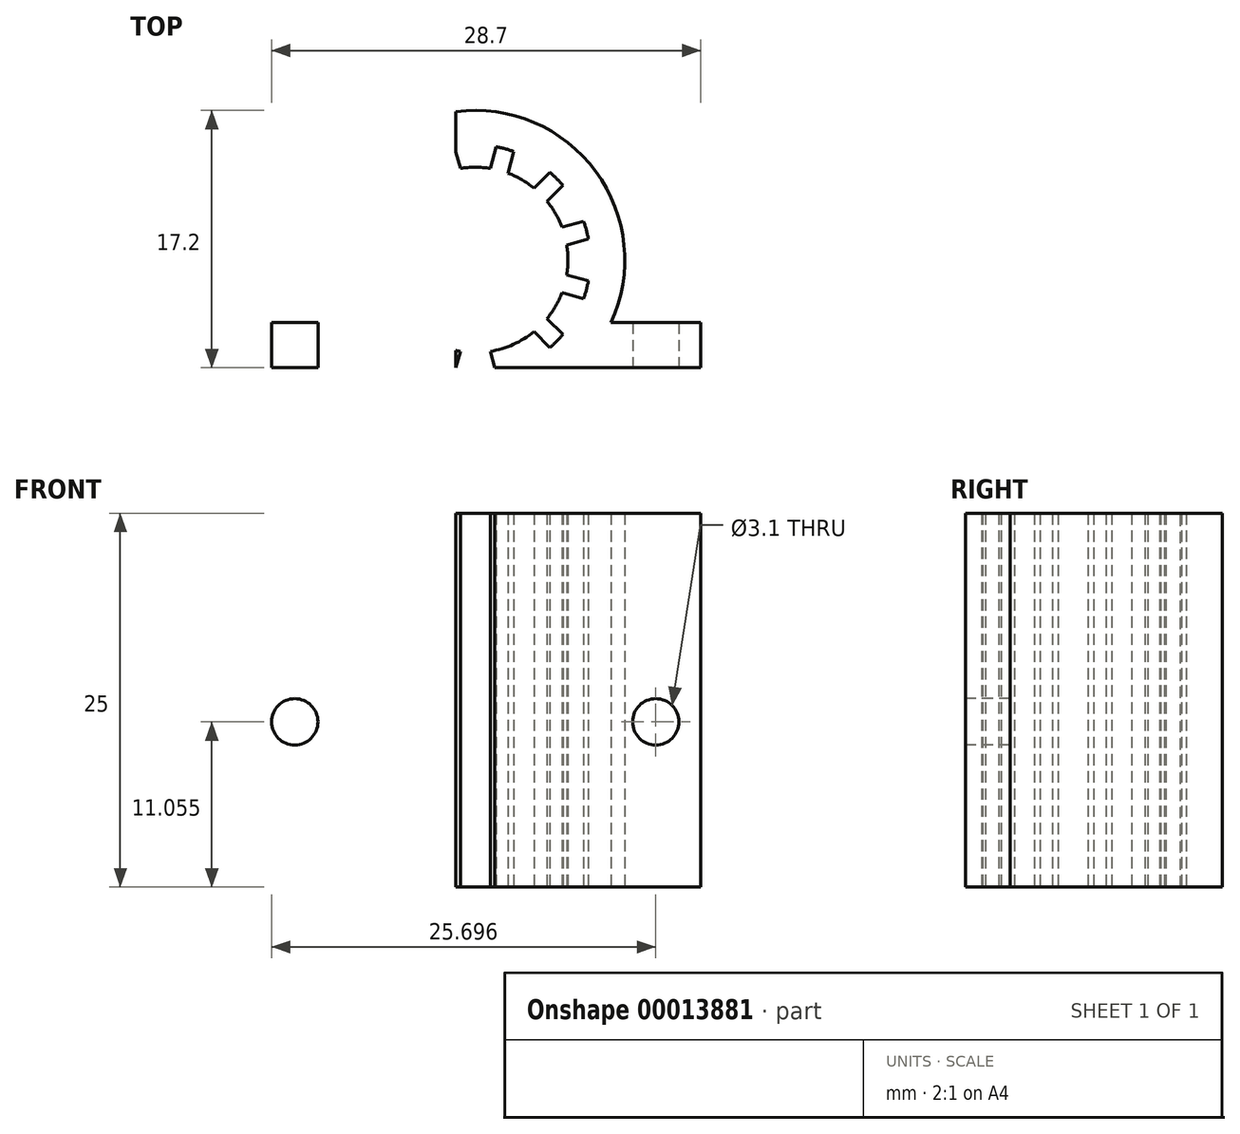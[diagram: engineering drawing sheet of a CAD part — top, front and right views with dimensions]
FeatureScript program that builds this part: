
annotation { "Feature Type Name" : "Feature", "Feature Type Description" : "" }
export const myFeature = defineFeature(function(context is Context, id is Id, definition is map)
    precondition{}
    {
        {
            var Q0;
            Q0=qCreatedBy(makeId("Top.planeOp"),FACE);
            var sketch = newSketch(context, id + "F0", { "sketchPlane" : qUnion([Q0])});
            skCircle(sketch, "E0", {"center": v(-45.8, 26.19) * mm, "radius": 10 * mm});
            skCircle(sketch, "E1", {"center": v(-45.8, 26.19) * mm, "radius": 6.2 * mm});
            skLineSegment(sketch, "E2", {"start": v(-53.65, 19.99) * mm, "end": v(-37.95, 19.99) * mm, "construction": true});
            skLineSegment(sketch, "E3", {"start": v(-45.8, 19.99) * mm, "end": v(-45.8, 38.7) * mm, "construction": true});
            skLineSegment(sketch, "E4", {"start": v(-47.19, 33.76) * mm, "end": v(-46.8, 32.3) * mm});
            skCircle(sketch, "E5", {"center": v(-45.8, 26.19) * mm, "radius": 7.7 * mm, "construction": true});
            skLineSegment(sketch, "E6.MirrorCS", {"start": v(-44.41, 33.76) * mm, "end": v(-44.8, 32.3) * mm});
            skCircle(sketch, "E7.MirrorC", {"center": v(-45.8, 26.19) * mm, "radius": 7.7 * mm});
            skLineSegment(sketch, "E8.1.0", {"start": v(-50.79, 32.05) * mm, "end": v(-49.72, 30.99) * mm});
            skLineSegment(sketch, "E8.1.1", {"start": v(-48.38, 33.44) * mm, "end": v(-48, 31.99) * mm});
            skLineSegment(sketch, "E8.2.0", {"start": v(-53.05, 28.77) * mm, "end": v(-51.6, 28.38) * mm});
            skLineSegment(sketch, "E8.2.1", {"start": v(-51.66, 31.17) * mm, "end": v(-50.6, 30.11) * mm});
            skLineSegment(sketch, "E8.3.0", {"start": v(-53.37, 24.8) * mm, "end": v(-51.92, 25.19) * mm});
            skLineSegment(sketch, "E8.3.1", {"start": v(-53.37, 27.58) * mm, "end": v(-51.92, 27.19) * mm});
            skLineSegment(sketch, "E8.4.0", {"start": v(-51.66, 21.2) * mm, "end": v(-50.6, 22.26) * mm});
            skLineSegment(sketch, "E8.4.1", {"start": v(-53.05, 23.6) * mm, "end": v(-51.6, 24) * mm});
            skLineSegment(sketch, "E8.5.0", {"start": v(-48.38, 18.94) * mm, "end": v(-48, 20.39) * mm});
            skLineSegment(sketch, "E8.5.1", {"start": v(-50.79, 20.33) * mm, "end": v(-49.72, 21.39) * mm});
            skLineSegment(sketch, "E8.6.0", {"start": v(-44.41, 18.62) * mm, "end": v(-44.8, 20.07) * mm});
            skLineSegment(sketch, "E8.6.1", {"start": v(-47.19, 18.62) * mm, "end": v(-46.8, 20.07) * mm});
            skLineSegment(sketch, "E8.7.0", {"start": v(-40.81, 20.33) * mm, "end": v(-41.87, 21.39) * mm});
            skLineSegment(sketch, "E8.7.1", {"start": v(-43.22, 18.94) * mm, "end": v(-43.6, 20.39) * mm});
            skLineSegment(sketch, "E9", {"start": v(-52.74, 18.99) * mm, "end": v(-38.86, 18.99) * mm});
            skLineSegment(sketch, "E10", {"start": v(-52.74, 18.99) * mm, "end": v(-60.87, 18.99) * mm});
            skLineSegment(sketch, "E11", {"start": v(-60.87, 18.99) * mm, "end": v(-60.87, 21.99) * mm});
            skLineSegment(sketch, "E12", {"start": v(-60.87, 21.99) * mm, "end": v(-54.87, 21.99) * mm});
            skLineSegment(sketch, "E13.MirrorCS", {"start": v(-30.72, 21.99) * mm, "end": v(-36.72, 21.99) * mm});
            skLineSegment(sketch, "E14.MirrorCS", {"start": v(-30.72, 18.99) * mm, "end": v(-30.72, 21.99) * mm});
            skLineSegment(sketch, "E15.MirrorCS", {"start": v(-38.86, 18.99) * mm, "end": v(-30.72, 18.99) * mm});
            skLineSegment(sketch, "E16.2.8.0", {"start": v(-38.55, 23.6) * mm, "end": v(-40, 24) * mm});
            skLineSegment(sketch, "E16.3.8.0", {"start": v(-39.94, 21.2) * mm, "end": v(-41, 22.26) * mm});
            skLineSegment(sketch, "E16.2.9.0", {"start": v(-38.23, 27.58) * mm, "end": v(-39.68, 27.19) * mm});
            skLineSegment(sketch, "E16.3.9.0", {"start": v(-38.23, 24.8) * mm, "end": v(-39.68, 25.19) * mm});
            skLineSegment(sketch, "E16.2.10.0", {"start": v(-39.94, 31.17) * mm, "end": v(-41, 30.11) * mm});
            skLineSegment(sketch, "E16.3.10.0", {"start": v(-38.55, 28.77) * mm, "end": v(-40, 28.38) * mm});
            skLineSegment(sketch, "E16.2.11.0", {"start": v(-43.22, 33.44) * mm, "end": v(-43.6, 31.99) * mm});
            skLineSegment(sketch, "E16.3.11.0", {"start": v(-40.81, 32.05) * mm, "end": v(-41.87, 30.99) * mm});
            skSolve(sketch);
        }
        {
            var Q0;
            {var subQ1=sQuery(id+"F0.wireOp",EDGE,"E10");Q0=makeQuery(id+"F0.imprint","IMPRINT",FACE,{"disambiguationData":[TD([[makeQuery(id+"F0.imprint","IMPRINT",EDGE,{"derivedFrom":subQ1}),-1.0]])]});}
            var Q1;
            {var subQ3=sQuery(id+"F0.wireOp",EDGE,"E0");var subQ8=makeQuery(id+"F0.imprint","INTERSECT",VERTEX,{"derivedFrom":[subQ3,sQuery(id+"F0.wireOp",EDGE,"E12")]});Q1=makeQuery(id+"F0.imprint","IMPRINT",FACE,{"disambiguationData":[TD([[makeQuery(id+"F0.imprint","IMPRINT",EDGE,{"disambiguationData":[TD([[subQ8,1.0]])],"derivedFrom":subQ3}),1.0]])]});}
            var Q2;
            {var subQ1=sQuery(id+"F0.wireOp",EDGE,"E13.MirrorCS");Q2=makeQuery(id+"F0.imprint","IMPRINT",FACE,{"disambiguationData":[TD([[makeQuery(id+"F0.imprint","IMPRINT",EDGE,{"derivedFrom":subQ1}),1.0]])]});}
            var Q3;
            {var subQ1=sQuery(id+"F0.wireOp",EDGE,"E8.4.0");Q3=makeQuery(id+"F0.imprint","IMPRINT",FACE,{"disambiguationData":[TD([[makeQuery(id+"F0.imprint","IMPRINT",EDGE,{"derivedFrom":subQ1}),1.0]])]});}
            var Q4;
            {var subQ1=sQuery(id+"F0.wireOp",EDGE,"E8.3.0");Q4=makeQuery(id+"F0.imprint","IMPRINT",FACE,{"disambiguationData":[TD([[makeQuery(id+"F0.imprint","IMPRINT",EDGE,{"derivedFrom":subQ1}),1.0]])]});}
            var Q5;
            {var subQ1=sQuery(id+"F0.wireOp",EDGE,"E8.2.0");Q5=makeQuery(id+"F0.imprint","IMPRINT",FACE,{"disambiguationData":[TD([[makeQuery(id+"F0.imprint","IMPRINT",EDGE,{"derivedFrom":subQ1}),1.0]])]});}
            var Q6;
            {var subQ1=sQuery(id+"F0.wireOp",EDGE,"E8.1.0");Q6=makeQuery(id+"F0.imprint","IMPRINT",FACE,{"disambiguationData":[TD([[makeQuery(id+"F0.imprint","IMPRINT",EDGE,{"derivedFrom":subQ1}),1.0]])]});}
            var Q7;
            {var subQ2=sQuery(id+"F0.wireOp",EDGE,"E4");Q7=makeQuery(id+"F0.imprint","IMPRINT",FACE,{"disambiguationData":[TD([[makeQuery(id+"F0.imprint","IMPRINT",EDGE,{"derivedFrom":subQ2}),1.0]])]});}
            var Q8;
            {var subQ1=sQuery(id+"F0.wireOp",EDGE,"E16.2.11.0");Q8=makeQuery(id+"F0.imprint","IMPRINT",FACE,{"disambiguationData":[TD([[makeQuery(id+"F0.imprint","IMPRINT",EDGE,{"derivedFrom":subQ1}),1.0]])]});}
            var Q9;
            {var subQ1=sQuery(id+"F0.wireOp",EDGE,"E16.2.10.0");Q9=makeQuery(id+"F0.imprint","IMPRINT",FACE,{"disambiguationData":[TD([[makeQuery(id+"F0.imprint","IMPRINT",EDGE,{"derivedFrom":subQ1}),1.0]])]});}
            var Q10;
            {var subQ1=sQuery(id+"F0.wireOp",EDGE,"E16.2.9.0");Q10=makeQuery(id+"F0.imprint","IMPRINT",FACE,{"disambiguationData":[TD([[makeQuery(id+"F0.imprint","IMPRINT",EDGE,{"derivedFrom":subQ1}),1.0]])]});}
            var Q11;
            {var subQ1=sQuery(id+"F0.wireOp",EDGE,"E16.2.8.0");Q11=makeQuery(id+"F0.imprint","IMPRINT",FACE,{"disambiguationData":[TD([[makeQuery(id+"F0.imprint","IMPRINT",EDGE,{"derivedFrom":subQ1}),1.0]])]});}
            var Q12;
            {var subQ7=sQuery(id+"F0.wireOp",EDGE,"E8.7.0");Q12=makeQuery(id+"F0.imprint","IMPRINT",FACE,{"disambiguationData":[TD([[makeQuery(id+"F0.imprint","IMPRINT",EDGE,{"derivedFrom":subQ7}),1.0]])]});}
            var Q13;
            {var subQ5=sQuery(id+"F0.wireOp",EDGE,"E8.5.1");Q13=makeQuery(id+"F0.imprint","IMPRINT",FACE,{"disambiguationData":[TD([[makeQuery(id+"F0.imprint","IMPRINT",EDGE,{"derivedFrom":subQ5}),-1.0]])]});}
            var Q14;
            {var subQ3=sQuery(id+"F0.wireOp",EDGE,"E8.6.0");var subQ5=sQuery(id+"F0.wireOp",EDGE,"E1");var subQ7=makeQuery(id+"F0.imprint","INTERSECT",VERTEX,{"derivedFrom":[subQ5,subQ3]});Q14=makeQuery(id+"F0.imprint","IMPRINT",FACE,{"disambiguationData":[TD([[makeQuery(id+"F0.imprint","IMPRINT",EDGE,{"disambiguationData":[TD([[subQ7,-1.0]])],"derivedFrom":subQ5}),-1.0]])]});}
            var Q15;
            {var subQ3=sQuery(id+"F0.wireOp",EDGE,"E8.5.0");var subQ5=sQuery(id+"F0.wireOp",EDGE,"E1");var subQ7=makeQuery(id+"F0.imprint","INTERSECT",VERTEX,{"derivedFrom":[subQ5,subQ3]});Q15=makeQuery(id+"F0.imprint","IMPRINT",FACE,{"disambiguationData":[TD([[makeQuery(id+"F0.imprint","IMPRINT",EDGE,{"disambiguationData":[TD([[subQ7,-1.0]])],"derivedFrom":subQ5}),-1.0]])]});}
            extrude(context, id + "F1", {"entities" : qUnion([Q0, Q1, Q2, Q3, Q4, Q5, Q6, Q7, Q8, Q9, Q10, Q11, Q12, Q13, Q14, Q15]), "depth" : 25 * mm});
        }
        {
            var Q0;
            Q0=makeQuery(id+"F1.opExtrude","SWEPT_FACE",FACE,{"disambiguationData":[OSD([sQuery(id+"F0.wireOp",EDGE,"E9"),sQuery(id+"F0.wireOp",EDGE,"E10")])]});
            var sketch = newSketch(context, id + "F2", { "sketchPlane" : qUnion([Q0])});
            skLineSegment(sketch, "E17.0", {"start": v(-44.8, 25) * mm, "end": v(-46.8, 25) * mm});
            skLineSegment(sketch, "E18", {"start": v(-45.8, 25) * mm, "end": v(-45.8, 35.27) * mm, "construction": true});
            skCircle(sketch, "E19", {"center": v(-57.87, 21.07) * mm, "radius": 1.55 * mm});
            skLineSegment(sketch, "E20.0", {"start": v(-60.87, 25) * mm, "end": v(-54.87, 25) * mm});
            skLineSegment(sketch, "E21", {"start": v(-57.87, 25) * mm, "end": v(-57.87, 21.07) * mm, "construction": true});
            skCircle(sketch, "E22.MirrorC", {"center": v(-33.72, 21.07) * mm, "radius": 1.55 * mm});
            skLineSegment(sketch, "E23", {"start": v(-60.87, 16.06) * mm, "end": v(-36.05, 16.06) * mm, "construction": true});
            skCircle(sketch, "E24.MirrorC", {"center": v(-57.87, 11.06) * mm, "radius": 1.55 * mm});
            skCircle(sketch, "E25.MirrorC", {"center": v(-33.72, 11.06) * mm, "radius": 1.55 * mm});
            skSolve(sketch);
        }
        {
            var Q0;
            Q0=makeQuery(id+"F2.imprint","IMPRINT",FACE,{"disambiguationData":[TD([[makeQuery(id+"F2.imprint","IMPRINT",EDGE,{"derivedFrom":sQuery(id+"F2.wireOp",EDGE,"E19")}),1.0]])]});
            var Q1;
            Q1=makeQuery(id+"F2.imprint","IMPRINT",FACE,{"disambiguationData":[TD([[makeQuery(id+"F2.imprint","IMPRINT",EDGE,{"derivedFrom":sQuery(id+"F2.wireOp",EDGE,"E22.MirrorC")}),-1.0]])]});
            var Q2;
            Q2=makeQuery(id+"F2.imprint","IMPRINT",FACE,{"disambiguationData":[TD([[makeQuery(id+"F2.imprint","IMPRINT",EDGE,{"derivedFrom":sQuery(id+"F2.wireOp",EDGE,"E25.MirrorC")}),1.0]])]});
            var Q3;
            Q3=makeQuery(id+"F2.imprint","IMPRINT",FACE,{"disambiguationData":[TD([[makeQuery(id+"F2.imprint","IMPRINT",EDGE,{"derivedFrom":sQuery(id+"F2.wireOp",EDGE,"E24.MirrorC")}),-1.0]])]});
            extrude(context, id + "F3", {"entities" : qUnion([Q0, Q1, Q2, Q3]), "operationType" : NewBodyOperationType.REMOVE, "oppositeDirection" : true, "depth" : 25 * mm});
        }
    });
